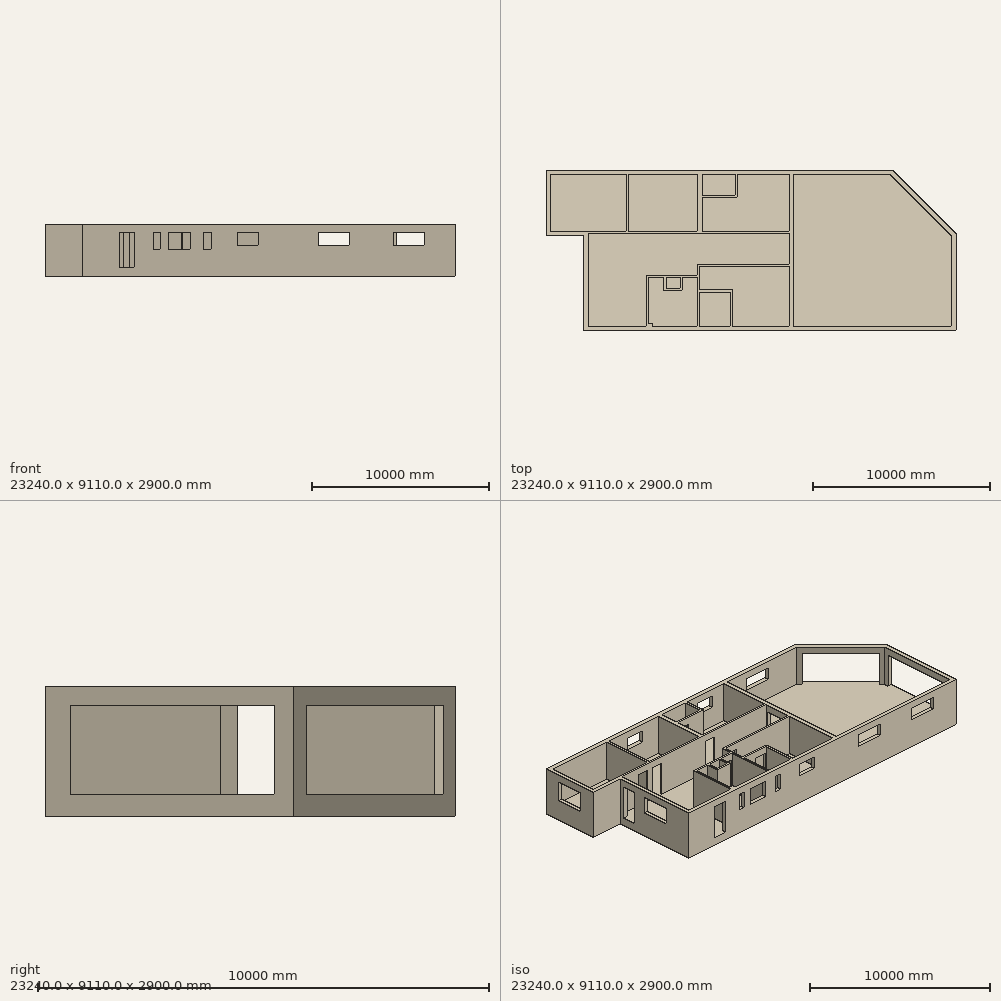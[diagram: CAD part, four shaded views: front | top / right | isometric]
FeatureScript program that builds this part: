
annotation { "Feature Type Name" : "Feature", "Feature Type Description" : "" }
export const myFeature = defineFeature(function(context is Context, id is Id, definition is map)
    precondition{}
    {
        {
            var Q0;
            Q0=qCreatedBy(makeId("Top.planeOp"),FACE);
            var sketch = newSketch(context, id + "F0", { "sketchPlane" : qUnion([Q0])});
            skLineSegment(sketch, "E0.bottom", {"start": v(-19524.79, 99.54) * mm, "end": v(105.21, 99.54) * mm});
            skLineSegment(sketch, "E0.top", {"start": v(-17404.79, -9010.46) * mm, "end": v(3715.21, -9010.46) * mm});
            skLineSegment(sketch, "E0.left", {"start": v(-17404.79, -3620.46) * mm, "end": v(-17404.79, -9010.46) * mm});
            skLineSegment(sketch, "E0.right", {"start": v(3715.21, -3510.46) * mm, "end": v(3715.21, -9010.46) * mm});
            skLineSegment(sketch, "E1", {"start": v(105.21, 99.54) * mm, "end": v(3715.21, -3510.46) * mm});
            skLineSegment(sketch, "E2", {"start": v(-19524.79, 99.54) * mm, "end": v(-19524.79, -3620.46) * mm});
            skLineSegment(sketch, "E3", {"start": v(-19524.79, -3620.46) * mm, "end": v(-17404.79, -3620.46) * mm});
            skLineSegment(sketch, "E4.bottom", {"start": v(-19270.79, -154.46) * mm, "end": v(-15010.79, -154.46) * mm});
            skLineSegment(sketch, "E4.top", {"start": v(-19270.79, -3366.46) * mm, "end": v(-15010.79, -3366.46) * mm});
            skLineSegment(sketch, "E4.left", {"start": v(-19270.79, -154.46) * mm, "end": v(-19270.79, -3366.46) * mm});
            skLineSegment(sketch, "E5.top", {"start": v(-17150.79, -8756.46) * mm, "end": v(-13855.76, -8756.46) * mm});
            skLineSegment(sketch, "E5.left", {"start": v(-17150.79, -3493.46) * mm, "end": v(-17150.79, -8756.46) * mm});
            skLineSegment(sketch, "E6", {"start": v(-17150.79, -3493.46) * mm, "end": v(-5778.79, -3493.46) * mm});
            skLineSegment(sketch, "E7", {"start": v(-15010.79, -154.46) * mm, "end": v(-15010.79, -3366.46) * mm});
            skLineSegment(sketch, "E8", {"start": v(-14883.79, -154.46) * mm, "end": v(-14883.79, -3366.46) * mm});
            skLineSegment(sketch, "E9", {"start": v(-10689.79, -154.46) * mm, "end": v(-10689.79, -1327.46) * mm});
            skLineSegment(sketch, "E10", {"start": v(-10943.79, -154.46) * mm, "end": v(-10943.79, -3366.46) * mm});
            skLineSegment(sketch, "E11", {"start": v(-5778.79, -154.46) * mm, "end": v(-5778.79, -3366.46) * mm});
            skLineSegment(sketch, "E12.trimOffspring", {"start": v(-10689.79, -3366.46) * mm, "end": v(-5778.79, -3366.46) * mm});
            skLineSegment(sketch, "E13.trimOffspring", {"start": v(-10689.79, -154.46) * mm, "end": v(-8816.79, -154.46) * mm});
            skLineSegment(sketch, "E14.trimOffspring", {"start": v(-5778.79, -3493.46) * mm, "end": v(-5778.79, -5229.46) * mm});
            skLineSegment(sketch, "E15.trimOffspring", {"start": v(-14883.79, -3366.46) * mm, "end": v(-10922.28, -3366.46) * mm});
            skLineSegment(sketch, "E16.trimOffspring", {"start": v(-14883.79, -154.46) * mm, "end": v(-10943.79, -154.46) * mm});
            skLineSegment(sketch, "E17", {"start": v(-5524.79, -154.46) * mm, "end": v(-29.58, -154.46) * mm});
            skLineSegment(sketch, "E18", {"start": v(-29.58, -154.46) * mm, "end": v(3431.63, -3615.67) * mm});
            skLineSegment(sketch, "E19", {"start": v(3431.63, -3615.67) * mm, "end": v(3431.63, -8756.46) * mm});
            skLineSegment(sketch, "E20", {"start": v(-5524.79, -8756.46) * mm, "end": v(3431.63, -8756.46) * mm});
            skLineSegment(sketch, "E21", {"start": v(-5524.79, -8756.46) * mm, "end": v(-5524.79, -154.46) * mm});
            skPoint(sketch, "E22.end.orphan", {"position": v(-17150.79, -6124.96) * mm});
            skPoint(sketch, "E22.start.orphan", {"position": v(-5778.79, -6124.96) * mm});
            skLineSegment(sketch, "E23", {"start": v(-5778.79, -5356.46) * mm, "end": v(-10841.76, -5356.46) * mm});
            skLineSegment(sketch, "E24", {"start": v(-5778.79, -5229.46) * mm, "end": v(-10968.76, -5229.46) * mm});
            skLineSegment(sketch, "E25", {"start": v(-10841.76, -5356.46) * mm, "end": v(-10841.76, -6691.03) * mm});
            skLineSegment(sketch, "E26", {"start": v(-10968.76, -5229.46) * mm, "end": v(-10968.76, -5856.46) * mm});
            skLineSegment(sketch, "E27.trimOffspring", {"start": v(-5778.79, -5356.46) * mm, "end": v(-5778.79, -8756.46) * mm});
            skLineSegment(sketch, "E28.trimOffspring", {"start": v(-10841.76, -8756.46) * mm, "end": v(-9091.76, -8756.46) * mm});
            skLineSegment(sketch, "E29", {"start": v(-10841.76, -6818.03) * mm, "end": v(-9091.76, -6818.03) * mm});
            skLineSegment(sketch, "E30", {"start": v(-9091.76, -6818.03) * mm, "end": v(-9091.76, -8756.46) * mm});
            skLineSegment(sketch, "E31", {"start": v(-10841.76, -6691.03) * mm, "end": v(-8964.76, -6691.03) * mm});
            skLineSegment(sketch, "E32", {"start": v(-8964.76, -6691.03) * mm, "end": v(-8964.76, -8756.46) * mm});
            skLineSegment(sketch, "E33.trimOffspring", {"start": v(-8964.76, -8756.46) * mm, "end": v(-5778.79, -8756.46) * mm});
            skLineSegment(sketch, "E34.trimOffspring", {"start": v(-10841.76, -6818.03) * mm, "end": v(-10841.76, -8756.46) * mm});
            skLineSegment(sketch, "E35", {"start": v(-13855.76, -8756.46) * mm, "end": v(-13855.76, -5856.46) * mm});
            skLineSegment(sketch, "E36", {"start": v(-13855.76, -5856.46) * mm, "end": v(-10968.76, -5856.46) * mm});
            skLineSegment(sketch, "E37", {"start": v(-13728.76, -8566.46) * mm, "end": v(-13728.76, -5983.46) * mm});
            skLineSegment(sketch, "E38", {"start": v(-13728.76, -5983.46) * mm, "end": v(-12868.76, -5983.46) * mm});
            skLineSegment(sketch, "E39.trimOffspring", {"start": v(-13498.76, -8756.46) * mm, "end": v(-10968.76, -8756.46) * mm});
            skLineSegment(sketch, "E40.trimOffspring", {"start": v(-10968.76, -5983.46) * mm, "end": v(-10968.76, -8756.46) * mm});
            skLineSegment(sketch, "E41", {"start": v(-11818.76, -5983.46) * mm, "end": v(-11818.76, -6733.46) * mm});
            skLineSegment(sketch, "E42", {"start": v(-11818.76, -6733.46) * mm, "end": v(-12868.76, -6733.46) * mm});
            skLineSegment(sketch, "E43", {"start": v(-12868.76, -6733.46) * mm, "end": v(-12868.76, -5983.46) * mm});
            skLineSegment(sketch, "E44", {"start": v(-12741.76, -5983.46) * mm, "end": v(-12741.76, -6606.46) * mm});
            skLineSegment(sketch, "E45", {"start": v(-12741.76, -6606.46) * mm, "end": v(-11945.76, -6606.46) * mm});
            skLineSegment(sketch, "E46", {"start": v(-11945.76, -6606.46) * mm, "end": v(-11945.76, -5983.46) * mm});
            skLineSegment(sketch, "E47.trimOffspring", {"start": v(-12741.76, -5983.46) * mm, "end": v(-11945.76, -5983.46) * mm});
            skLineSegment(sketch, "E48.trimOffspring", {"start": v(-11818.76, -5983.46) * mm, "end": v(-10968.76, -5983.46) * mm});
            skLineSegment(sketch, "E49", {"start": v(-8689.79, -154.46) * mm, "end": v(-8689.79, -1454.46) * mm});
            skLineSegment(sketch, "E50", {"start": v(-8689.79, -1454.46) * mm, "end": v(-10689.79, -1454.46) * mm});
            skLineSegment(sketch, "E51", {"start": v(-8816.79, -154.46) * mm, "end": v(-8816.79, -1327.46) * mm});
            skLineSegment(sketch, "E52", {"start": v(-8816.79, -1327.46) * mm, "end": v(-10689.79, -1327.46) * mm});
            skLineSegment(sketch, "E53.trimOffspring", {"start": v(-8689.79, -154.46) * mm, "end": v(-5778.79, -154.46) * mm});
            skLineSegment(sketch, "E54.trimOffspring", {"start": v(-10689.79, -1454.46) * mm, "end": v(-10689.79, -3366.46) * mm});
            skLineSegment(sketch, "E55", {"start": v(-13728.76, -8566.46) * mm, "end": v(-13498.76, -8566.46) * mm});
            skLineSegment(sketch, "E56", {"start": v(-13498.76, -8566.46) * mm, "end": v(-13498.76, -8756.46) * mm});
            skPoint(sketch, "E57.orphan", {"position": v(-13728.76, -8756.46) * mm});
            skSolve(sketch);
        }
        {
            var Q0;
            Q0=makeQuery(id+"F0.imprint","IMPRINT",FACE,{"disambiguationData":[TD([[makeQuery(id+"F0.imprint","IMPRINT",EDGE,{"derivedFrom":sQuery(id+"F0.wireOp",EDGE,"E0.bottom")}),-1.0]])]});
            extrude(context, id + "F1", {"entities" : qUnion([Q0]), "depth" : 2400 * mm, "hasSecondDirection" : true, "secondDirectionOppositeDirection" : true, "secondDirectionDepth" : 500 * mm});
        }
        {
            var Q0;
            Q0=makeQuery(id+"F1.opExtrude","SWEPT_FACE",FACE,{"disambiguationData":[OSD([sQuery(id+"F0.wireOp",EDGE,"E36")])]});
            var sketch = newSketch(context, id + "F2", { "sketchPlane" : qUnion([Q0])});
            skLineSegment(sketch, "E58.bottom", {"start": v(11768.76, 1980) * mm, "end": v(11018.76, 1980) * mm});
            skLineSegment(sketch, "E58.top", {"start": v(11768.76, 0) * mm, "end": v(11018.76, 0) * mm});
            skLineSegment(sketch, "E58.left", {"start": v(11768.76, 1980) * mm, "end": v(11768.76, 0) * mm});
            skLineSegment(sketch, "E58.right", {"start": v(11018.76, 1980) * mm, "end": v(11018.76, 0) * mm});
            skLineSegment(sketch, "E59.bottom", {"start": v(12718.76, -500) * mm, "end": v(11968.76, -500) * mm});
            skLineSegment(sketch, "E59.top", {"start": v(12718.76, 1480) * mm, "end": v(11968.76, 1480) * mm});
            skLineSegment(sketch, "E59.left", {"start": v(12718.76, -500) * mm, "end": v(12718.76, 1480) * mm});
            skLineSegment(sketch, "E59.right", {"start": v(11968.76, -500) * mm, "end": v(11968.76, 1480) * mm});
            skSolve(sketch);
        }
        {
            var Q0;
            Q0 = qSketchRegion(id + "F2", true);
            var Q1;
            Q1 = qSketchRegion(id + "Fb8nwodHZtpyVHM_1", true);
            extrude(context, id + "F3", {"entities" : qUnion([Q0, Q1]), "operationType" : NewBodyOperationType.REMOVE, "oppositeDirection" : true, "depth" : 250 * mm});
        }
        {
            var Q0;
            Q0=makeQuery(id+"F1.opExtrude","SWEPT_FACE",FACE,{"disambiguationData":[OSD([sQuery(id+"F0.wireOp",EDGE,"E6")])]});
            var sketch = newSketch(context, id + "F4", { "sketchPlane" : qUnion([Q0])});
            skLineSegment(sketch, "E60.bottom", {"start": v(-15860.79, 1980) * mm, "end": v(-15110.79, 1980) * mm});
            skLineSegment(sketch, "E60.top", {"start": v(-15860.79, 0) * mm, "end": v(-15110.79, 0) * mm});
            skLineSegment(sketch, "E60.left", {"start": v(-15860.79, 1980) * mm, "end": v(-15860.79, 0) * mm});
            skLineSegment(sketch, "E60.right", {"start": v(-15110.79, 1980) * mm, "end": v(-15110.79, 0) * mm});
            skLineSegment(sketch, "E61.bottom", {"start": v(-14783.79, 1980) * mm, "end": v(-14033.79, 1980) * mm});
            skLineSegment(sketch, "E61.top", {"start": v(-14783.79, 0) * mm, "end": v(-14033.79, 0) * mm});
            skLineSegment(sketch, "E61.left", {"start": v(-14783.79, 1980) * mm, "end": v(-14783.79, 0) * mm});
            skLineSegment(sketch, "E61.right", {"start": v(-14033.79, 1980) * mm, "end": v(-14033.79, 0) * mm});
            skLineSegment(sketch, "E62.bottom", {"start": v(-10589.79, 1980) * mm, "end": v(-9839.79, 1980) * mm});
            skLineSegment(sketch, "E62.top", {"start": v(-10589.79, 0) * mm, "end": v(-9839.79, 0) * mm});
            skLineSegment(sketch, "E62.left", {"start": v(-10589.79, 1980) * mm, "end": v(-10589.79, 0) * mm});
            skLineSegment(sketch, "E62.right", {"start": v(-9839.79, 1980) * mm, "end": v(-9839.79, 0) * mm});
            skSolve(sketch);
        }
        {
            var Q0;
            Q0 = qSketchRegion(id + "F4", true);
            extrude(context, id + "F5", {"entities" : qUnion([Q0]), "operationType" : NewBodyOperationType.REMOVE, "oppositeDirection" : true, "depth" : 500 * mm});
        }
        {
            var Q0;
            Q0=makeQuery(id+"F1.opExtrude","SWEPT_FACE",FACE,{"disambiguationData":[OSD([sQuery(id+"F0.wireOp",EDGE,"E23")])]});
            var sketch = newSketch(context, id + "F6", { "sketchPlane" : qUnion([Q0])});
            skLineSegment(sketch, "E63.bottom", {"start": v(-10741.76, 1980) * mm, "end": v(-9991.76, 1980) * mm});
            skLineSegment(sketch, "E63.top", {"start": v(-10741.76, 0) * mm, "end": v(-9991.76, 0) * mm});
            skLineSegment(sketch, "E63.left", {"start": v(-10741.76, 1980) * mm, "end": v(-10741.76, 0) * mm});
            skLineSegment(sketch, "E63.right", {"start": v(-9991.76, 1980) * mm, "end": v(-9991.76, 0) * mm});
            skSolve(sketch);
        }
        {
            var Q0;
            Q0 = qSketchRegion(id + "F6", true);
            extrude(context, id + "F7", {"entities" : qUnion([Q0]), "operationType" : NewBodyOperationType.REMOVE, "oppositeDirection" : true, "depth" : 500 * mm});
        }
        {
            var Q0;
            Q0=makeQuery(id+"F1.opExtrude","SWEPT_FACE",FACE,{"disambiguationData":[OSD([sQuery(id+"F0.wireOp",EDGE,"E14.trimOffspring")])]});
            var sketch = newSketch(context, id + "F8", { "sketchPlane" : qUnion([Q0])});
            skLineSegment(sketch, "E64.bottom", {"start": v(5111.46, 1980) * mm, "end": v(3611.46, 1980) * mm});
            skLineSegment(sketch, "E64.top", {"start": v(5111.46, 0) * mm, "end": v(3611.46, 0) * mm});
            skLineSegment(sketch, "E64.left", {"start": v(5111.46, 1980) * mm, "end": v(5111.46, 0) * mm});
            skLineSegment(sketch, "E64.right", {"start": v(3611.46, 1980) * mm, "end": v(3611.46, 0) * mm});
            skSolve(sketch);
        }
        {
            var Q0;
            Q0 = qSketchRegion(id + "F8", true);
            extrude(context, id + "F9", {"entities" : qUnion([Q0]), "operationType" : NewBodyOperationType.REMOVE, "oppositeDirection" : true, "depth" : 500 * mm});
        }
        {
            var Q0;
            Q0=makeQuery(id+"F1.opExtrude","CAP_FACE",FACE,{"disambiguationData":[OSD([sQuery(id+"F0.wireOp",EDGE,"E0.bottom"),sQuery(id+"F0.wireOp",EDGE,"E0.top"),sQuery(id+"F0.wireOp",EDGE,"E0.left"),sQuery(id+"F0.wireOp",EDGE,"E0.right"),sQuery(id+"F0.wireOp",EDGE,"E1"),sQuery(id+"F0.wireOp",EDGE,"E2"),sQuery(id+"F0.wireOp",EDGE,"E3"),sQuery(id+"F0.wireOp",EDGE,"E4.bottom"),sQuery(id+"F0.wireOp",EDGE,"E4.top"),sQuery(id+"F0.wireOp",EDGE,"E4.left"),sQuery(id+"F0.wireOp",EDGE,"E5.top"),sQuery(id+"F0.wireOp",EDGE,"E5.left"),sQuery(id+"F0.wireOp",EDGE,"E6"),sQuery(id+"F0.wireOp",EDGE,"E7"),sQuery(id+"F0.wireOp",EDGE,"E8"),sQuery(id+"F0.wireOp",EDGE,"E9"),sQuery(id+"F0.wireOp",EDGE,"E10"),sQuery(id+"F0.wireOp",EDGE,"E11"),sQuery(id+"F0.wireOp",EDGE,"E12.trimOffspring"),sQuery(id+"F0.wireOp",EDGE,"E13.trimOffspring"),sQuery(id+"F0.wireOp",EDGE,"E14.trimOffspring"),sQuery(id+"F0.wireOp",EDGE,"E15.trimOffspring"),sQuery(id+"F0.wireOp",EDGE,"E16.trimOffspring"),sQuery(id+"F0.wireOp",EDGE,"E17"),sQuery(id+"F0.wireOp",EDGE,"E18"),sQuery(id+"F0.wireOp",EDGE,"E19"),sQuery(id+"F0.wireOp",EDGE,"E20"),sQuery(id+"F0.wireOp",EDGE,"E21"),sQuery(id+"F0.wireOp",EDGE,"E23"),sQuery(id+"F0.wireOp",EDGE,"E24"),sQuery(id+"F0.wireOp",EDGE,"E25"),sQuery(id+"F0.wireOp",EDGE,"E26"),sQuery(id+"F0.wireOp",EDGE,"E27.trimOffspring"),sQuery(id+"F0.wireOp",EDGE,"E28.trimOffspring"),sQuery(id+"F0.wireOp",EDGE,"E29"),sQuery(id+"F0.wireOp",EDGE,"E30"),sQuery(id+"F0.wireOp",EDGE,"E31"),sQuery(id+"F0.wireOp",EDGE,"E32"),sQuery(id+"F0.wireOp",EDGE,"E33.trimOffspring"),sQuery(id+"F0.wireOp",EDGE,"E34.trimOffspring"),sQuery(id+"F0.wireOp",EDGE,"E35"),sQuery(id+"F0.wireOp",EDGE,"E36"),sQuery(id+"F0.wireOp",EDGE,"E37"),sQuery(id+"F0.wireOp",EDGE,"E38"),sQuery(id+"F0.wireOp",EDGE,"E39.trimOffspring"),sQuery(id+"F0.wireOp",EDGE,"E40.trimOffspring"),sQuery(id+"F0.wireOp",EDGE,"E41"),sQuery(id+"F0.wireOp",EDGE,"E42"),sQuery(id+"F0.wireOp",EDGE,"E43"),sQuery(id+"F0.wireOp",EDGE,"E44"),sQuery(id+"F0.wireOp",EDGE,"E45"),sQuery(id+"F0.wireOp",EDGE,"E46"),sQuery(id+"F0.wireOp",EDGE,"E47.trimOffspring"),sQuery(id+"F0.wireOp",EDGE,"E48.trimOffspring")])],"isStart":true});
            var sketch = newSketch(context, id + "F10", { "sketchPlane" : qUnion([Q0])});
            skSolve(sketch);
        }
        {
            var Q0;
            {var subQ2=sQuery(id+"F0.wireOp",EDGE,"E0.bottom");Q0=makeQuery(id+"F10.imprint","IMPRINT",FACE,{"disambiguationData":[TD([[makeQuery(id+"F10.imprint","IMPRINT",EDGE,{"derivedFrom":makeQuery(id+"F1.opExtrude","CAP_EDGE",EDGE,{"disambiguationData":[OSD([subQ2])],"isStart":true})}),1.0]])]});}
            var sketch = newSketch(context, id + "F11", { "sketchPlane" : qUnion([Q0])});
            skLineSegment(sketch, "E65", {"start": v(3715.21, 9010.46) * mm, "end": v(3715.21, 3510.46) * mm});
            skLineSegment(sketch, "E66", {"start": v(3715.21, 3510.46) * mm, "end": v(105.21, -99.54) * mm});
            skLineSegment(sketch, "E67", {"start": v(105.21, -99.54) * mm, "end": v(-19524.79, -99.54) * mm});
            skLineSegment(sketch, "E68", {"start": v(-19524.79, -99.54) * mm, "end": v(-19524.79, 3620.46) * mm});
            skLineSegment(sketch, "E69", {"start": v(-19524.79, 3620.46) * mm, "end": v(-17404.79, 3620.46) * mm});
            skLineSegment(sketch, "E70", {"start": v(-17404.79, 3620.46) * mm, "end": v(-17404.79, 9010.46) * mm});
            skLineSegment(sketch, "E71", {"start": v(-17404.79, 9010.46) * mm, "end": v(3715.21, 9010.46) * mm});
            skSolve(sketch);
        }
        {
            var Q0;
            Q0 = qSketchRegion(id + "F11", true);
            extrude(context, id + "F12", {"entities" : qUnion([Q0]), "operationType" : NewBodyOperationType.ADD, "oppositeDirection" : true, "depth" : 500 * mm});
        }
        {
            var Q0;
            Q0=makeQuery(id+"F1.opExtrude","SWEPT_FACE",FACE,{"disambiguationData":[OSD([sQuery(id+"F0.wireOp",EDGE,"E29")])]});
            var sketch = newSketch(context, id + "F13", { "sketchPlane" : qUnion([Q0])});
            skLineSegment(sketch, "E72.bottom", {"start": v(-9941.76, 0) * mm, "end": v(-9191.76, 0) * mm});
            skLineSegment(sketch, "E72.top", {"start": v(-9941.76, 1980) * mm, "end": v(-9191.76, 1980) * mm});
            skLineSegment(sketch, "E72.left", {"start": v(-9941.76, 0) * mm, "end": v(-9941.76, 1980) * mm});
            skLineSegment(sketch, "E72.right", {"start": v(-9191.76, 0) * mm, "end": v(-9191.76, 1980) * mm});
            skSolve(sketch);
        }
        {
            var Q0;
            Q0 = qSketchRegion(id + "F13", true);
            extrude(context, id + "F14", {"entities" : qUnion([Q0]), "operationType" : NewBodyOperationType.REMOVE, "oppositeDirection" : true, "depth" : 500 * mm});
        }
        {
            var Q0;
            Q0=makeQuery(id+"F1.opExtrude","SWEPT_FACE",FACE,{"disambiguationData":[OSD([sQuery(id+"F0.wireOp",EDGE,"E5.left")])]});
            var sketch = newSketch(context, id + "F15", { "sketchPlane" : qUnion([Q0])});
            skLineSegment(sketch, "E73.bottom", {"start": v(-7256.46, 980) * mm, "end": v(-5506.46, 980) * mm});
            skLineSegment(sketch, "E73.top", {"start": v(-7256.46, 1980) * mm, "end": v(-5506.46, 1980) * mm});
            skLineSegment(sketch, "E73.left", {"start": v(-7256.46, 980) * mm, "end": v(-7256.46, 1980) * mm});
            skLineSegment(sketch, "E73.right", {"start": v(-5506.46, 980) * mm, "end": v(-5506.46, 1980) * mm});
            skLineSegment(sketch, "E74.bottom", {"start": v(-4743.46, 1980) * mm, "end": v(-3893.46, 1980) * mm});
            skLineSegment(sketch, "E74.top", {"start": v(-4743.46, 0) * mm, "end": v(-3893.46, 0) * mm});
            skLineSegment(sketch, "E74.left", {"start": v(-4743.46, 1980) * mm, "end": v(-4743.46, 0) * mm});
            skLineSegment(sketch, "E74.right", {"start": v(-3893.46, 1980) * mm, "end": v(-3893.46, 0) * mm});
            skSolve(sketch);
        }
        {
            var Q0;
            Q0 = qSketchRegion(id + "F15", true);
            extrude(context, id + "F16", {"entities" : qUnion([Q0]), "operationType" : NewBodyOperationType.REMOVE, "endBound" : BoundingType.THROUGH_ALL, "oppositeDirection" : true, "depth" : 500 * mm});
        }
        {
            var Q0;
            Q0=makeQuery(id+"F1.opExtrude","SWEPT_FACE",FACE,{"disambiguationData":[OSD([sQuery(id+"F0.wireOp",EDGE,"E4.left")])]});
            var sketch = newSketch(context, id + "F17", { "sketchPlane" : qUnion([Q0])});
            skLineSegment(sketch, "E75.bottom", {"start": v(-2616.46, 1950) * mm, "end": v(-866.46, 1950) * mm});
            skLineSegment(sketch, "E75.top", {"start": v(-2616.46, 750) * mm, "end": v(-866.46, 750) * mm});
            skLineSegment(sketch, "E75.left", {"start": v(-2616.46, 1950) * mm, "end": v(-2616.46, 750) * mm});
            skLineSegment(sketch, "E75.right", {"start": v(-866.46, 1950) * mm, "end": v(-866.46, 750) * mm});
            skSolve(sketch);
        }
        {
            var Q0;
            Q0 = qSketchRegion(id + "F17", true);
            extrude(context, id + "F18", {"entities" : qUnion([Q0]), "operationType" : NewBodyOperationType.REMOVE, "endBound" : BoundingType.THROUGH_ALL, "oppositeDirection" : true, "depth" : 25 * mm});
        }
        {
            var Q0;
            Q0=makeQuery(id+"F1.opExtrude","SWEPT_FACE",FACE,{"disambiguationData":[OSD([sQuery(id+"F0.wireOp",EDGE,"E5.top")])]});
            var sketch = newSketch(context, id + "F19", { "sketchPlane" : qUnion([Q0])});
            skLineSegment(sketch, "E76.bottom", {"start": v(15355.76, 1980) * mm, "end": v(14505.76, 1980) * mm});
            skLineSegment(sketch, "E76.top", {"start": v(15355.76, 0) * mm, "end": v(14505.76, 0) * mm});
            skLineSegment(sketch, "E76.left", {"start": v(15355.76, 1980) * mm, "end": v(15355.76, 0) * mm});
            skLineSegment(sketch, "E76.right", {"start": v(14505.76, 1980) * mm, "end": v(14505.76, 0) * mm});
            skSolve(sketch);
        }
        {
            var Q0;
            Q0 = qSketchRegion(id + "F19", true);
            extrude(context, id + "F20", {"entities" : qUnion([Q0]), "operationType" : NewBodyOperationType.REMOVE, "endBound" : BoundingType.THROUGH_ALL, "oppositeDirection" : true, "depth" : 25 * mm});
        }
        {
            var Q0;
            Q0=makeQuery(id+"F1.opExtrude","SWEPT_FACE",FACE,{"disambiguationData":[OSD([sQuery(id+"F0.wireOp",EDGE,"E39.trimOffspring")])]});
            var sketch = newSketch(context, id + "F21", { "sketchPlane" : qUnion([Q0])});
            skLineSegment(sketch, "E77.bottom", {"start": v(13028.76, 1980) * mm, "end": v(13428.76, 1980) * mm});
            skLineSegment(sketch, "E77.top", {"start": v(13028.76, 980) * mm, "end": v(13428.76, 980) * mm});
            skLineSegment(sketch, "E77.left", {"start": v(13028.76, 1980) * mm, "end": v(13028.76, 980) * mm});
            skLineSegment(sketch, "E77.right", {"start": v(13428.76, 1980) * mm, "end": v(13428.76, 980) * mm});
            skLineSegment(sketch, "E78.bottom", {"start": v(11328.76, 1980) * mm, "end": v(12528.76, 1980) * mm});
            skLineSegment(sketch, "E78.top", {"start": v(11328.76, 980) * mm, "end": v(12528.76, 980) * mm});
            skLineSegment(sketch, "E78.left", {"start": v(11328.76, 1980) * mm, "end": v(11328.76, 980) * mm});
            skLineSegment(sketch, "E78.right", {"start": v(12528.76, 1980) * mm, "end": v(12528.76, 980) * mm});
            skPoint(sketch, "E79.oppositeSnap0", {"position": v(10968.76, 1200) * mm});
            skLineSegment(sketch, "E79.bottom", {"start": v(10141.76, 1980) * mm, "end": v(10541.76, 1980) * mm});
            skLineSegment(sketch, "E79.left", {"start": v(10141.76, 1980) * mm, "end": v(10141.76, 980) * mm});
            skLineSegment(sketch, "E79.right", {"start": v(10541.76, 1980) * mm, "end": v(10541.76, 980) * mm});
            skLineSegment(sketch, "E80.bottom", {"start": v(7464.76, 1980) * mm, "end": v(8664.76, 1980) * mm});
            skLineSegment(sketch, "E80.top", {"start": v(7464.76, 1230) * mm, "end": v(8664.76, 1230) * mm});
            skLineSegment(sketch, "E80.left", {"start": v(7464.76, 1980) * mm, "end": v(7464.76, 1230) * mm});
            skLineSegment(sketch, "E80.right", {"start": v(8664.76, 1980) * mm, "end": v(8664.76, 1230) * mm});
            skLineSegment(sketch, "E81.bottom", {"start": v(2274.79, 1980) * mm, "end": v(4024.79, 1980) * mm});
            skLineSegment(sketch, "E81.top", {"start": v(2274.79, 1230) * mm, "end": v(4024.79, 1230) * mm});
            skLineSegment(sketch, "E81.left", {"start": v(2274.79, 1980) * mm, "end": v(2274.79, 1230) * mm});
            skLineSegment(sketch, "E81.right", {"start": v(4024.79, 1980) * mm, "end": v(4024.79, 1230) * mm});
            skLineSegment(sketch, "E82.bottom", {"start": v(-1931.63, 1980) * mm, "end": v(-181.63, 1980) * mm});
            skLineSegment(sketch, "E82.top", {"start": v(-1931.63, 1230) * mm, "end": v(-181.63, 1230) * mm});
            skLineSegment(sketch, "E82.left", {"start": v(-1931.63, 1980) * mm, "end": v(-1931.63, 1230) * mm});
            skLineSegment(sketch, "E82.right", {"start": v(-181.63, 1980) * mm, "end": v(-181.63, 1230) * mm});
            skLineSegment(sketch, "E83", {"start": v(10541.76, 980) * mm, "end": v(10141.76, 980) * mm});
            skPoint(sketch, "E79.top.end.orphan", {"position": v(10541.76, 1200) * mm});
            skSolve(sketch);
        }
        {
            var Q0;
            Q0 = qSketchRegion(id + "F21", true);
            extrude(context, id + "F22", {"entities" : qUnion([Q0]), "operationType" : NewBodyOperationType.REMOVE, "endBound" : BoundingType.THROUGH_ALL, "oppositeDirection" : true, "depth" : 25 * mm});
        }
        {
            var Q0;
            Q0=makeQuery(id+"F1.opExtrude","SWEPT_FACE",FACE,{"disambiguationData":[OSD([sQuery(id+"F0.wireOp",EDGE,"E16.trimOffspring")])]});
            var sketch = newSketch(context, id + "F23", { "sketchPlane" : qUnion([Q0])});
            skLineSegment(sketch, "E84.bottom", {"start": v(-13383.79, 1980) * mm, "end": v(-12183.79, 1980) * mm});
            skLineSegment(sketch, "E84.top", {"start": v(-13383.79, 1230) * mm, "end": v(-12183.79, 1230) * mm});
            skLineSegment(sketch, "E84.left", {"start": v(-13383.79, 1980) * mm, "end": v(-13383.79, 1230) * mm});
            skLineSegment(sketch, "E84.right", {"start": v(-12183.79, 1980) * mm, "end": v(-12183.79, 1230) * mm});
            skLineSegment(sketch, "E85.bottom", {"start": v(-7878.79, 1980) * mm, "end": v(-6678.79, 1980) * mm});
            skLineSegment(sketch, "E85.top", {"start": v(-7878.79, 1230) * mm, "end": v(-6678.79, 1230) * mm});
            skLineSegment(sketch, "E85.left", {"start": v(-7878.79, 1980) * mm, "end": v(-7878.79, 1230) * mm});
            skLineSegment(sketch, "E85.right", {"start": v(-6678.79, 1980) * mm, "end": v(-6678.79, 1230) * mm});
            skLineSegment(sketch, "E86.bottom", {"start": v(-4024.79, 1980) * mm, "end": v(-2274.79, 1980) * mm});
            skLineSegment(sketch, "E86.top", {"start": v(-4024.79, 1230) * mm, "end": v(-2274.79, 1230) * mm});
            skLineSegment(sketch, "E86.left", {"start": v(-4024.79, 1980) * mm, "end": v(-4024.79, 1230) * mm});
            skLineSegment(sketch, "E86.right", {"start": v(-2274.79, 1980) * mm, "end": v(-2274.79, 1230) * mm});
            skSolve(sketch);
        }
        {
            var Q0;
            Q0 = qSketchRegion(id + "F23", true);
            extrude(context, id + "F24", {"entities" : qUnion([Q0]), "operationType" : NewBodyOperationType.REMOVE, "endBound" : BoundingType.THROUGH_ALL, "oppositeDirection" : true, "depth" : 25 * mm});
        }
        {
            var Q0;
            Q0=makeQuery(id+"F1.opExtrude","SWEPT_FACE",FACE,{"disambiguationData":[OSD([sQuery(id+"F0.wireOp",EDGE,"E18")])]});
            var sketch = newSketch(context, id + "F25", { "sketchPlane" : qUnion([Q0])});
            skLineSegment(sketch, "E87.bottom", {"start": v(388.3, 1980) * mm, "end": v(4683.2, 1980) * mm});
            skLineSegment(sketch, "E87.top", {"start": v(388.3, 0) * mm, "end": v(4683.2, 0) * mm});
            skLineSegment(sketch, "E87.left", {"start": v(388.3, 1980) * mm, "end": v(388.3, 0) * mm});
            skLineSegment(sketch, "E87.right", {"start": v(4683.2, 1980) * mm, "end": v(4683.2, 0) * mm});
            skSolve(sketch);
        }
        {
            var Q0;
            Q0 = qSketchRegion(id + "F25", true);
            extrude(context, id + "F26", {"entities" : qUnion([Q0]), "operationType" : NewBodyOperationType.REMOVE, "endBound" : BoundingType.THROUGH_ALL, "oppositeDirection" : true, "depth" : 25 * mm});
        }
        {
            var Q0;
            Q0=makeQuery(id+"F1.opExtrude","SWEPT_FACE",FACE,{"disambiguationData":[OSD([sQuery(id+"F0.wireOp",EDGE,"E19")])]});
            var sketch = newSketch(context, id + "F27", { "sketchPlane" : qUnion([Q0])});
            skLineSegment(sketch, "E88.bottom", {"start": v(3915.67, 1980) * mm, "end": v(8456.46, 1980) * mm});
            skLineSegment(sketch, "E88.top", {"start": v(3915.67, 0) * mm, "end": v(8456.46, 0) * mm});
            skLineSegment(sketch, "E88.left", {"start": v(3915.67, 1980) * mm, "end": v(3915.67, 0) * mm});
            skLineSegment(sketch, "E88.right", {"start": v(8456.46, 1980) * mm, "end": v(8456.46, 0) * mm});
            skSolve(sketch);
        }
        {
            var Q0;
            Q0 = qSketchRegion(id + "F27", true);
            extrude(context, id + "F28", {"entities" : qUnion([Q0]), "operationType" : NewBodyOperationType.REMOVE, "endBound" : BoundingType.THROUGH_ALL, "oppositeDirection" : true, "depth" : 25 * mm});
        }
        {
            var Q0;
            Q0=makeQuery(id+"F1.opExtrude","SWEPT_FACE",FACE,{"disambiguationData":[OSD([sQuery(id+"F0.wireOp",EDGE,"E50")])]});
            var sketch = newSketch(context, id + "F29", { "sketchPlane" : qUnion([Q0])});
            skLineSegment(sketch, "E89.bottom", {"start": v(-10589.79, 1980) * mm, "end": v(-9839.79, 1980) * mm});
            skLineSegment(sketch, "E89.top", {"start": v(-10589.79, 0) * mm, "end": v(-9839.79, 0) * mm});
            skLineSegment(sketch, "E89.left", {"start": v(-10589.79, 1980) * mm, "end": v(-10589.79, 0) * mm});
            skLineSegment(sketch, "E89.right", {"start": v(-9839.79, 1980) * mm, "end": v(-9839.79, 0) * mm});
            skSolve(sketch);
        }
        {
            var Q0;
            Q0 = qSketchRegion(id + "F29", true);
            extrude(context, id + "F30", {"entities" : qUnion([Q0]), "operationType" : NewBodyOperationType.REMOVE, "oppositeDirection" : true, "depth" : 500 * mm});
        }
    });
